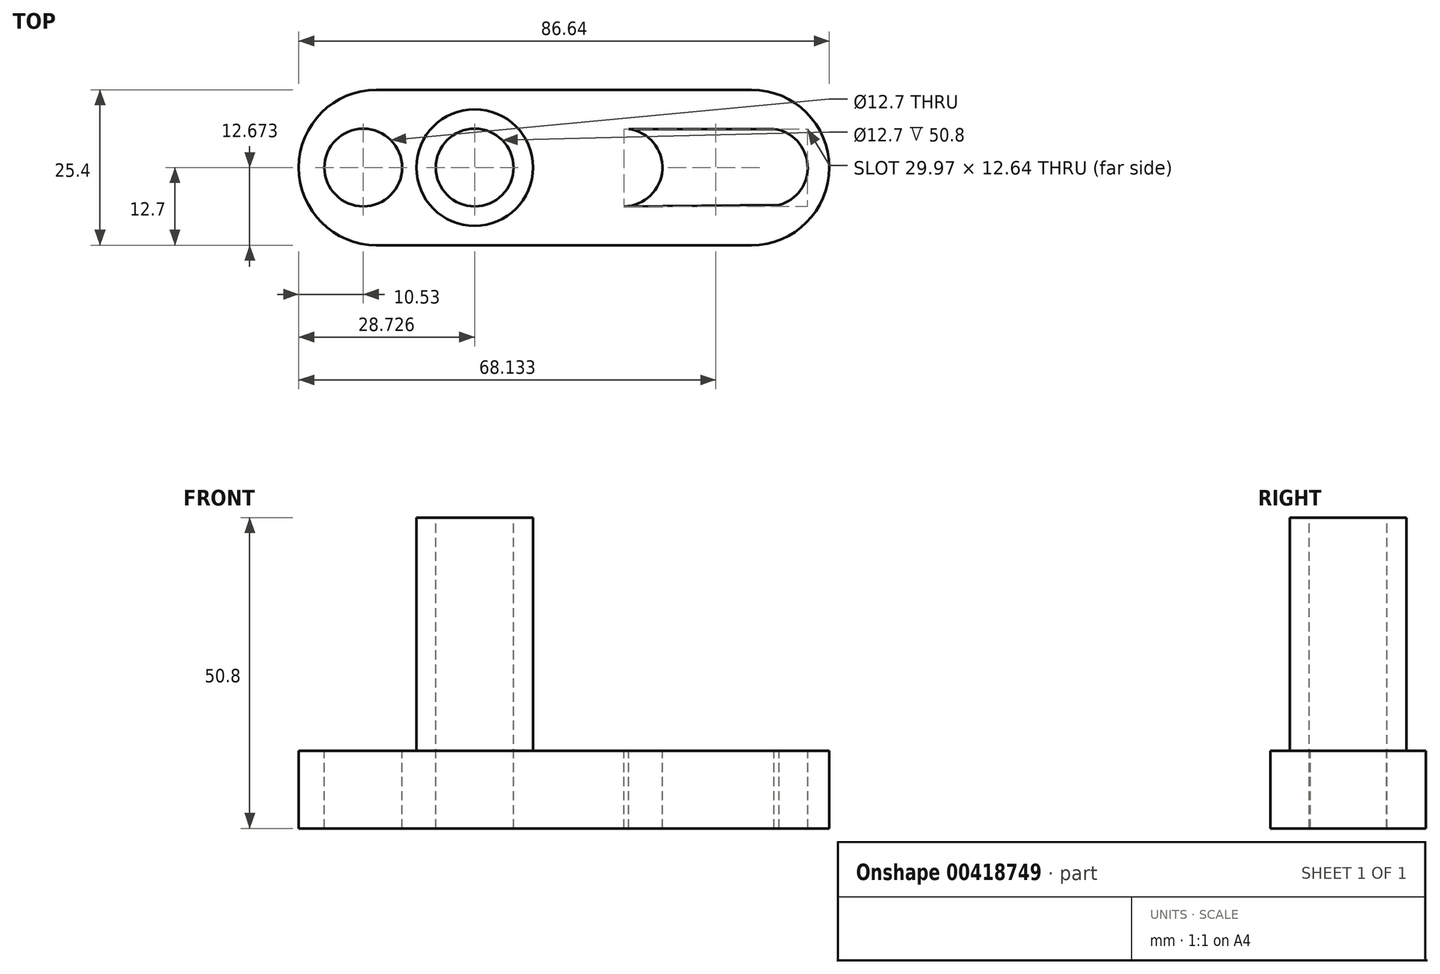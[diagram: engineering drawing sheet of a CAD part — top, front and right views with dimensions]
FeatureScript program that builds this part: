
annotation { "Feature Type Name" : "Feature", "Feature Type Description" : "" }
export const myFeature = defineFeature(function(context is Context, id is Id, definition is map)
    precondition{}
    {
        {
            var Q0;
            Q0=qCreatedBy(makeId("Front.planeOp"),FACE);
            var sketch = newSketch(context, id + "F0", { "sketchPlane" : qUnion([Q0])});
            skLineSegment(sketch, "E0", {"start": v(0, 0) * mm, "end": v(0, 12.7) * mm});
            skLineSegment(sketch, "E1", {"start": v(0, 12.7) * mm, "end": v(101.6, 12.7) * mm});
            skLineSegment(sketch, "E2", {"start": v(101.6, 12.7) * mm, "end": v(101.6, 0) * mm});
            skLineSegment(sketch, "E3", {"start": v(101.6, 0) * mm, "end": v(0, 0) * mm});
            skSolve(sketch);
        }
        {
            var Q0;
            Q0=makeQuery(id+"F0.imprint","IMPRINT",FACE,{"disambiguationData":[TD([[makeQuery(id+"F0.imprint","IMPRINT",EDGE,{"derivedFrom":sQuery(id+"F0.wireOp",EDGE,"E0")}),-1.0]])]});
            extrude(context, id + "F1", {"entities" : qUnion([Q0]), "depth" : 25.4 * mm});
        }
        {
            var Q0;
            Q0=makeQuery(id+"F1.opExtrude","SWEPT_FACE",FACE,{"disambiguationData":[OSD([sQuery(id+"F0.wireOp",EDGE,"E1")])]});
            var sketch = newSketch(context, id + "F2", { "sketchPlane" : qUnion([Q0])});
            skCircle(sketch, "E4", {"center": v(12.7, -12.7) * mm, "radius": 6.35 * mm});
            skSolve(sketch);
        }
        {
            var Q0;
            Q0=makeQuery(id+"F2.imprint","IMPRINT",FACE,{"disambiguationData":[TD([[makeQuery(id+"F2.imprint","IMPRINT",EDGE,{"derivedFrom":sQuery(id+"F2.wireOp",EDGE,"E4")}),1.0]])]});
            extrude(context, id + "F3", {"entities" : qUnion([Q0]), "operationType" : NewBodyOperationType.REMOVE, "oppositeDirection" : true, "depth" : 25.4 * mm});
        }
        {
            var Q0;
            Q0=makeQuery(id+"F1.opExtrude","SWEPT_FACE",FACE,{"disambiguationData":[OSD([sQuery(id+"F0.wireOp",EDGE,"E1")])]});
            var sketch = newSketch(context, id + "F4", { "sketchPlane" : qUnion([Q0])});
            skCircle(sketch, "E5", {"center": v(30.9, -12.7) * mm, "radius": 9.53 * mm});
            skSolve(sketch);
        }
        {
            var Q0;
            Q0=makeQuery(id+"F4.imprint","IMPRINT",FACE,{"disambiguationData":[TD([[makeQuery(id+"F4.imprint","IMPRINT",EDGE,{"derivedFrom":sQuery(id+"F4.wireOp",EDGE,"E5")}),1.0]])]});
            extrude(context, id + "F5", {"entities" : qUnion([Q0]), "operationType" : NewBodyOperationType.ADD, "depth" : 38.1 * mm});
        }
        {
            var Q0;
            Q0=makeQuery(id+"F5.opExtrude","CAP_FACE",FACE,{"disambiguationData":[OSD([sQuery(id+"F4.wireOp",EDGE,"E5")])],"isStart":false});
            var sketch = newSketch(context, id + "F6", { "sketchPlane" : qUnion([Q0])});
            skCircle(sketch, "E6", {"center": v(30.9, -12.7) * mm, "radius": 6.35 * mm});
            skSolve(sketch);
        }
        {
            var Q0;
            Q0=makeQuery(id+"F6.imprint","IMPRINT",FACE,{"disambiguationData":[TD([[makeQuery(id+"F6.imprint","IMPRINT",EDGE,{"derivedFrom":sQuery(id+"F6.wireOp",EDGE,"E6")}),1.0]])]});
            extrude(context, id + "F7", {"entities" : qUnion([Q0]), "operationType" : NewBodyOperationType.REMOVE, "oppositeDirection" : true, "depth" : 50.8 * mm});
        }
        {
            var Q0;
            Q0=makeQuery(id+"F1.opExtrude","SWEPT_FACE",FACE,{"disambiguationData":[OSD([sQuery(id+"F0.wireOp",EDGE,"E1")])]});
            var sketch = newSketch(context, id + "F8", { "sketchPlane" : qUnion([Q0])});
            skCircle(sketch, "E7", {"center": v(55.2, -12.7) * mm, "radius": 6.35 * mm});
            skCircle(sketch, "E8", {"center": v(78.95, -12.7) * mm, "radius": 6.35 * mm});
            skLineSegment(sketch, "E9", {"start": v(54.38, -6.4) * mm, "end": v(79.78, -6.4) * mm});
            skLineSegment(sketch, "E10", {"start": v(55.2, -19.05) * mm, "end": v(80.6, -18.83) * mm});
            skSolve(sketch);
        }
        {
            var Q0;
            {var subQ1=sQuery(id+"F8.wireOp",EDGE,"E7");var subQ3=makeQuery(id+"F8.imprint","IMPRINT",VERTEX,{"derivedFrom":subQ1});Q0=makeQuery(id+"F8.imprint","IMPRINT",FACE,{"disambiguationData":[TD([[makeQuery(id+"F8.imprint","IMPRINT",EDGE,{"disambiguationData":[TD([[subQ3,1.0]])],"derivedFrom":subQ1}),1.0]])]});}
            var Q1;
            {var subQ0=sQuery(id+"F8.wireOp",EDGE,"E10");var subQ1=sQuery(id+"F8.wireOp",EDGE,"E7");var subQ2=makeQuery(id+"F8.imprint","INTERSECT",VERTEX,{"derivedFrom":[subQ1,subQ0]});Q1=makeQuery(id+"F8.imprint","IMPRINT",FACE,{"disambiguationData":[TD([[makeQuery(id+"F8.imprint","IMPRINT",EDGE,{"disambiguationData":[TD([[subQ2,-1.0]])],"derivedFrom":subQ1}),-1.0]])]});}
            var Q2;
            {var subQ0=sQuery(id+"F8.wireOp",EDGE,"E9");var subQ1=sQuery(id+"F8.wireOp",EDGE,"E8");var subQ2=makeQuery(id+"F8.imprint","INTERSECT",VERTEX,{"disambiguationData":[OD(1.0)],"derivedFrom":[subQ1,subQ0]});Q2=makeQuery(id+"F8.imprint","IMPRINT",FACE,{"disambiguationData":[TD([[makeQuery(id+"F8.imprint","IMPRINT",EDGE,{"disambiguationData":[TD([[subQ2,-1.0]])],"derivedFrom":subQ1}),1.0]])]});}
            extrude(context, id + "F9", {"entities" : qUnion([Q0, Q1, Q2]), "operationType" : NewBodyOperationType.REMOVE, "oppositeDirection" : true, "depth" : 25.4 * mm});
        }
        {
            var Q0;
            Q0=makeQuery(id+"F1.opExtrude","SWEPT_FACE",FACE,{"disambiguationData":[OSD([sQuery(id+"F0.wireOp",EDGE,"E1")])]});
            var sketch = newSketch(context, id + "F10", { "sketchPlane" : qUnion([Q0])});
            skArc(sketch, "E11", {"start": v(76.1, -25.4) * mm, "mid": v(88.8, -12.7) * mm, "end": v(76.1, 0) * mm});
            skSolve(sketch);
        }
        {
            var Q0;
            {var subQ0=sQuery(id+"F10.wireOp",EDGE,"E11");Q0=makeQuery(id+"F10.imprint","IMPRINT",FACE,{"disambiguationData":[TD([[makeQuery(id+"F10.imprint","IMPRINT",EDGE,{"derivedFrom":subQ0}),-1.0]])]});}
            extrude(context, id + "F11", {"entities" : qUnion([Q0]), "operationType" : NewBodyOperationType.REMOVE, "oppositeDirection" : true, "depth" : 25.4 * mm});
        }
        {
            var Q0;
            Q0=makeQuery(id+"F1.opExtrude","SWEPT_FACE",FACE,{"disambiguationData":[OSD([sQuery(id+"F0.wireOp",EDGE,"E1")])]});
            var sketch = newSketch(context, id + "F12", { "sketchPlane" : qUnion([Q0])});
            skArc(sketch, "E12", {"start": v(14.87, 0) * mm, "mid": v(2.17, -12.7) * mm, "end": v(14.87, -25.4) * mm});
            skSolve(sketch);
        }
        {
            var Q0;
            {var subQ0=sQuery(id+"F12.wireOp",EDGE,"E12");Q0=makeQuery(id+"F12.imprint","IMPRINT",FACE,{"disambiguationData":[TD([[makeQuery(id+"F12.imprint","IMPRINT",EDGE,{"derivedFrom":subQ0}),-1.0]])]});}
            extrude(context, id + "F13", {"entities" : qUnion([Q0]), "operationType" : NewBodyOperationType.REMOVE, "oppositeDirection" : true, "depth" : 25.4 * mm});
        }
    });
